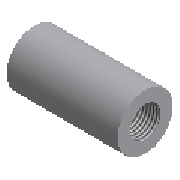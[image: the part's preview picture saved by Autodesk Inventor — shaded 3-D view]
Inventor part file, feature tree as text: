
AUTODESK INVENTOR PART (.ipt)
format: ipt  version: 2023 (Build 270158000, 158)  size: 165,376 bytes
history: native  units: mm (DEFAULTED — no unit token found)
features: other x6, sketch x1, revolve x1
ambient origin geometry x8: Origin, YZ Plane, XZ Plane, XY Plane, X Axis, Y Axis, Z Axis, Center Point
bodies: Solid1 (feature_tree)
feature tree (8):
  sketch  "Sketch1"  dims[d6=90.0deg d0=18.320766mm d1=47.752mm d2=28.448mm d16=25.4mm d17=0.0mm d18=25.4mm d19=0.0mm d3=0.312398mm d4=13.55598mm]
  revolve  "Revolve1"  [1 undecoded]
  other  "Work Point1"
  other  "Work Point2"
  other  "Work Axis1"
  other  "Work Point3"
  other  "Work Axis2"
  other  "Work Point4"
note: 1 required parameter value undecoded (feature->parameter linkage not recoverable at this tier; creation-order binding heuristic only, values carry confidence <= 0.55)
